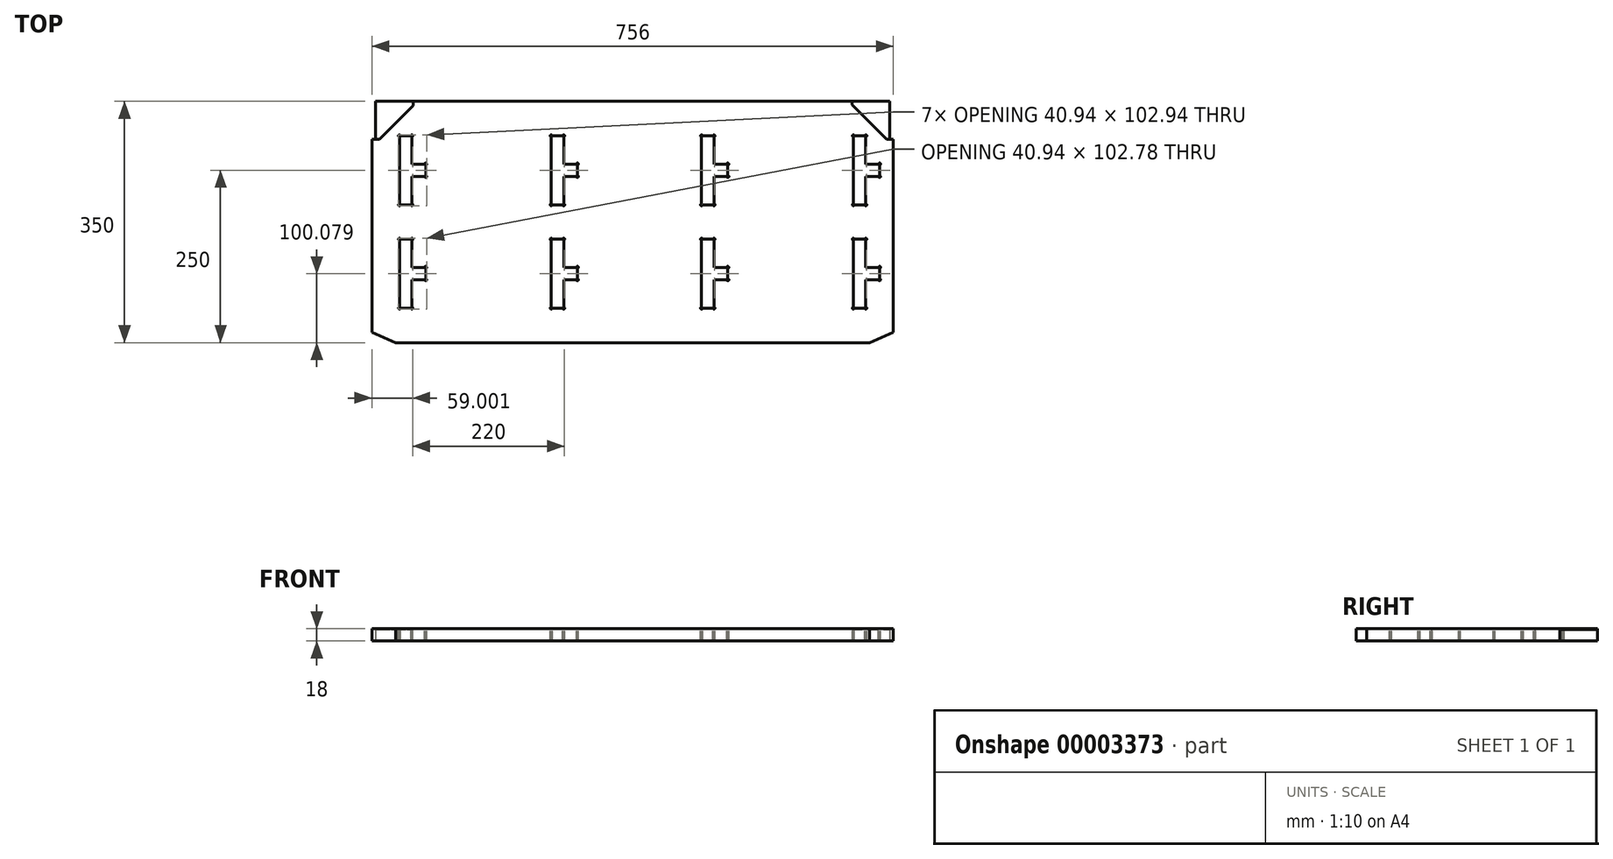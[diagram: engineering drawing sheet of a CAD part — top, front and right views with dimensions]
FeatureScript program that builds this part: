
annotation { "Feature Type Name" : "Feature", "Feature Type Description" : "" }
export const myFeature = defineFeature(function(context is Context, id is Id, definition is map)
    precondition{}
    {
        {
            var Q0;
            Q0=qCreatedBy(makeId("Top.planeOp"),FACE);
            var sketch = newSketch(context, id + "F0", { "sketchPlane" : qUnion([Q0])});
            skLineSegment(sketch, "E0.bottom", {"start": v(-425.74, -50) * mm, "end": v(330.26, -50) * mm});
            skLineSegment(sketch, "E0.top", {"start": v(-420.74, 300) * mm, "end": v(325.26, 300) * mm});
            skLineSegment(sketch, "E0.left", {"start": v(-425.74, -50) * mm, "end": v(-425.74, 245) * mm});
            skLineSegment(sketch, "E0.right", {"start": v(330.26, -50) * mm, "end": v(330.26, 245) * mm});
            skLineSegment(sketch, "E1.bottom", {"start": v(-165.74, 0) * mm, "end": v(-147.74, 0) * mm});
            skLineSegment(sketch, "E1.top", {"start": v(-165.74, 100) * mm, "end": v(-147.74, 100) * mm});
            skLineSegment(sketch, "E1.left", {"start": v(-165.74, 0) * mm, "end": v(-165.74, 100) * mm});
            skLineSegment(sketch, "E1.right", {"start": v(-147.74, 0) * mm, "end": v(-147.74, 41.16) * mm});
            skLineSegment(sketch, "E2.bottom", {"start": v(-165.74, 150) * mm, "end": v(-147.74, 150) * mm});
            skLineSegment(sketch, "E2.top", {"start": v(-165.74, 250) * mm, "end": v(-147.74, 250) * mm});
            skLineSegment(sketch, "E2.left", {"start": v(-165.74, 150) * mm, "end": v(-165.74, 250) * mm});
            skLineSegment(sketch, "E2.right", {"start": v(-147.74, 150) * mm, "end": v(-147.74, 191) * mm});
            skLineSegment(sketch, "E3.bottom", {"start": v(290.26, 0) * mm, "end": v(272.26, 0) * mm});
            skLineSegment(sketch, "E3.top", {"start": v(290.26, 100) * mm, "end": v(272.26, 100) * mm});
            skLineSegment(sketch, "E3.left", {"start": v(290.26, 0) * mm, "end": v(290.26, 41.16) * mm});
            skLineSegment(sketch, "E3.right", {"start": v(272.26, 0) * mm, "end": v(272.26, 100) * mm});
            skLineSegment(sketch, "E4.bottom", {"start": v(272.26, 250) * mm, "end": v(290.26, 250) * mm});
            skLineSegment(sketch, "E4.top", {"start": v(272.26, 150) * mm, "end": v(290.26, 150) * mm});
            skLineSegment(sketch, "E4.left", {"start": v(272.26, 250) * mm, "end": v(272.26, 150) * mm});
            skLineSegment(sketch, "E4.right", {"start": v(290.26, 250) * mm, "end": v(290.26, 209) * mm});
            skLineSegment(sketch, "E5.bottom", {"start": v(52.26, 100) * mm, "end": v(70.26, 100) * mm});
            skLineSegment(sketch, "E5.top", {"start": v(52.26, 0) * mm, "end": v(70.26, 0) * mm});
            skLineSegment(sketch, "E5.left", {"start": v(52.26, 100) * mm, "end": v(52.26, 0) * mm});
            skLineSegment(sketch, "E5.right", {"start": v(70.26, 100) * mm, "end": v(70.26, 59.16) * mm});
            skLineSegment(sketch, "E6.bottom", {"start": v(52.26, 250) * mm, "end": v(70.26, 250) * mm});
            skLineSegment(sketch, "E6.top", {"start": v(52.26, 150) * mm, "end": v(70.26, 150) * mm});
            skLineSegment(sketch, "E6.left", {"start": v(52.26, 250) * mm, "end": v(52.26, 150) * mm});
            skLineSegment(sketch, "E6.right", {"start": v(70.26, 250) * mm, "end": v(70.26, 209) * mm});
            skLineSegment(sketch, "E7.bottom", {"start": v(-385.74, 0.16) * mm, "end": v(-367.74, 0.16) * mm});
            skLineSegment(sketch, "E7.top", {"start": v(-385.74, 100) * mm, "end": v(-367.74, 100) * mm});
            skLineSegment(sketch, "E7.left", {"start": v(-385.74, 0.16) * mm, "end": v(-385.74, 100) * mm});
            skLineSegment(sketch, "E7.right", {"start": v(-367.74, 0.16) * mm, "end": v(-367.74, 41.16) * mm});
            skLineSegment(sketch, "E8.bottom", {"start": v(-385.74, 150) * mm, "end": v(-367.74, 150) * mm});
            skLineSegment(sketch, "E8.top", {"start": v(-385.74, 250) * mm, "end": v(-367.74, 250) * mm});
            skLineSegment(sketch, "E8.left", {"start": v(-385.74, 150) * mm, "end": v(-385.74, 250) * mm});
            skLineSegment(sketch, "E8.right", {"start": v(-367.74, 150) * mm, "end": v(-367.74, 191) * mm});
            skLineSegment(sketch, "E9.bottom", {"start": v(-367.74, 41.16) * mm, "end": v(-347.74, 41.16) * mm});
            skLineSegment(sketch, "E9.top", {"start": v(-367.74, 59.16) * mm, "end": v(-347.74, 59.16) * mm});
            skLineSegment(sketch, "E9.right", {"start": v(-347.74, 41.16) * mm, "end": v(-347.74, 59.16) * mm});
            skLineSegment(sketch, "E10.bottom", {"start": v(-367.74, 191) * mm, "end": v(-347.74, 191) * mm});
            skLineSegment(sketch, "E10.top", {"start": v(-367.74, 209) * mm, "end": v(-347.74, 209) * mm});
            skLineSegment(sketch, "E10.right", {"start": v(-347.74, 191) * mm, "end": v(-347.74, 209) * mm});
            skLineSegment(sketch, "E11.trimOffspring", {"start": v(-367.74, 59.16) * mm, "end": v(-367.74, 100) * mm});
            skLineSegment(sketch, "E12.trimOffspring", {"start": v(-367.74, 209) * mm, "end": v(-367.74, 250) * mm});
            skLineSegment(sketch, "E13.bottom", {"start": v(-147.74, 41.16) * mm, "end": v(-127.74, 41.16) * mm});
            skLineSegment(sketch, "E13.top", {"start": v(-147.74, 59.16) * mm, "end": v(-127.74, 59.16) * mm});
            skLineSegment(sketch, "E13.right", {"start": v(-127.74, 41.16) * mm, "end": v(-127.74, 59.16) * mm});
            skLineSegment(sketch, "E14.bottom", {"start": v(-147.74, 191) * mm, "end": v(-127.74, 191) * mm});
            skLineSegment(sketch, "E14.top", {"start": v(-147.74, 209) * mm, "end": v(-127.74, 209) * mm});
            skLineSegment(sketch, "E14.right", {"start": v(-127.74, 191) * mm, "end": v(-127.74, 209) * mm});
            skLineSegment(sketch, "E15.bottom", {"start": v(70.26, 41.16) * mm, "end": v(90.26, 41.16) * mm});
            skLineSegment(sketch, "E15.top", {"start": v(70.26, 59.16) * mm, "end": v(90.26, 59.16) * mm});
            skLineSegment(sketch, "E15.right", {"start": v(90.26, 41.16) * mm, "end": v(90.26, 59.16) * mm});
            skLineSegment(sketch, "E16.bottom", {"start": v(70.26, 191) * mm, "end": v(90.26, 191) * mm});
            skLineSegment(sketch, "E16.top", {"start": v(70.26, 209) * mm, "end": v(90.26, 209) * mm});
            skLineSegment(sketch, "E16.right", {"start": v(90.26, 191) * mm, "end": v(90.26, 209) * mm});
            skLineSegment(sketch, "E17.bottom", {"start": v(290.26, 41.16) * mm, "end": v(310.26, 41.16) * mm});
            skLineSegment(sketch, "E17.top", {"start": v(290.26, 59.16) * mm, "end": v(310.26, 59.16) * mm});
            skLineSegment(sketch, "E17.right", {"start": v(310.26, 41.16) * mm, "end": v(310.26, 59.16) * mm});
            skLineSegment(sketch, "E18.bottom", {"start": v(290.26, 191) * mm, "end": v(310.26, 191) * mm});
            skLineSegment(sketch, "E18.top", {"start": v(290.26, 209) * mm, "end": v(310.26, 209) * mm});
            skLineSegment(sketch, "E18.right", {"start": v(310.26, 191) * mm, "end": v(310.26, 209) * mm});
            skLineSegment(sketch, "E19.trimOffspring", {"start": v(-147.74, 59.16) * mm, "end": v(-147.74, 100) * mm});
            skLineSegment(sketch, "E20.trimOffspring", {"start": v(-147.74, 209) * mm, "end": v(-147.74, 250) * mm});
            skLineSegment(sketch, "E21.trimOffspring", {"start": v(70.26, 191) * mm, "end": v(70.26, 150) * mm});
            skLineSegment(sketch, "E22.trimOffspring", {"start": v(70.26, 41.16) * mm, "end": v(70.26, 0) * mm});
            skLineSegment(sketch, "E23.trimOffspring", {"start": v(290.26, 59.16) * mm, "end": v(290.26, 100) * mm});
            skLineSegment(sketch, "E24.trimOffspring", {"start": v(290.26, 191) * mm, "end": v(290.26, 150) * mm});
            skLineSegment(sketch, "E25.top", {"start": v(-425.74, 245) * mm, "end": v(-420.74, 245) * mm});
            skLineSegment(sketch, "E25.right", {"start": v(-420.74, 300) * mm, "end": v(-420.74, 245) * mm});
            skLineSegment(sketch, "E26.top", {"start": v(330.26, 245) * mm, "end": v(325.26, 245) * mm});
            skLineSegment(sketch, "E26.right", {"start": v(325.26, 300) * mm, "end": v(325.26, 245) * mm});
            skSolve(sketch);
        }
        {
            var Q0;
            Q0=makeQuery(id+"F0.imprint","IMPRINT",FACE,{"disambiguationData":[TD([[makeQuery(id+"F0.imprint","IMPRINT",EDGE,{"derivedFrom":sQuery(id+"F0.wireOp",EDGE,"E0.bottom")}),1.0]])]});
            extrude(context, id + "F1", {"entities" : qUnion([Q0]), "depth" : 18 * mm});
        }
        {
            var Q0;
            Q0=makeQuery(id+"F1.opExtrude","CAP_FACE",FACE,{"disambiguationData":[OSD([sQuery(id+"F0.wireOp",EDGE,"E0.bottom"),sQuery(id+"F0.wireOp",EDGE,"E0.top"),sQuery(id+"F0.wireOp",EDGE,"E0.left"),sQuery(id+"F0.wireOp",EDGE,"E0.right"),sQuery(id+"F0.wireOp",EDGE,"E1.bottom"),sQuery(id+"F0.wireOp",EDGE,"E1.top"),sQuery(id+"F0.wireOp",EDGE,"E1.left"),sQuery(id+"F0.wireOp",EDGE,"E1.right"),sQuery(id+"F0.wireOp",EDGE,"E2.bottom"),sQuery(id+"F0.wireOp",EDGE,"E2.top"),sQuery(id+"F0.wireOp",EDGE,"E2.left"),sQuery(id+"F0.wireOp",EDGE,"E2.right"),sQuery(id+"F0.wireOp",EDGE,"E3.bottom"),sQuery(id+"F0.wireOp",EDGE,"E3.top"),sQuery(id+"F0.wireOp",EDGE,"E3.left"),sQuery(id+"F0.wireOp",EDGE,"E3.right"),sQuery(id+"F0.wireOp",EDGE,"E4.bottom"),sQuery(id+"F0.wireOp",EDGE,"E4.top"),sQuery(id+"F0.wireOp",EDGE,"E4.left"),sQuery(id+"F0.wireOp",EDGE,"E4.right"),sQuery(id+"F0.wireOp",EDGE,"E5.bottom"),sQuery(id+"F0.wireOp",EDGE,"E5.top"),sQuery(id+"F0.wireOp",EDGE,"E5.left"),sQuery(id+"F0.wireOp",EDGE,"E5.right"),sQuery(id+"F0.wireOp",EDGE,"E6.bottom"),sQuery(id+"F0.wireOp",EDGE,"E6.top"),sQuery(id+"F0.wireOp",EDGE,"E6.left"),sQuery(id+"F0.wireOp",EDGE,"E6.right"),sQuery(id+"F0.wireOp",EDGE,"E7.bottom"),sQuery(id+"F0.wireOp",EDGE,"E7.top"),sQuery(id+"F0.wireOp",EDGE,"E7.left"),sQuery(id+"F0.wireOp",EDGE,"E7.right"),sQuery(id+"F0.wireOp",EDGE,"E8.bottom"),sQuery(id+"F0.wireOp",EDGE,"E8.top"),sQuery(id+"F0.wireOp",EDGE,"E8.left"),sQuery(id+"F0.wireOp",EDGE,"E8.right"),sQuery(id+"F0.wireOp",EDGE,"E9.bottom"),sQuery(id+"F0.wireOp",EDGE,"E9.top"),sQuery(id+"F0.wireOp",EDGE,"E9.right"),sQuery(id+"F0.wireOp",EDGE,"E10.bottom"),sQuery(id+"F0.wireOp",EDGE,"E10.top"),sQuery(id+"F0.wireOp",EDGE,"E10.right"),sQuery(id+"F0.wireOp",EDGE,"E11.trimOffspring"),sQuery(id+"F0.wireOp",EDGE,"E12.trimOffspring"),sQuery(id+"F0.wireOp",EDGE,"E13.bottom"),sQuery(id+"F0.wireOp",EDGE,"E13.top"),sQuery(id+"F0.wireOp",EDGE,"E13.right"),sQuery(id+"F0.wireOp",EDGE,"E14.bottom"),sQuery(id+"F0.wireOp",EDGE,"E14.top"),sQuery(id+"F0.wireOp",EDGE,"E14.right"),sQuery(id+"F0.wireOp",EDGE,"E15.bottom"),sQuery(id+"F0.wireOp",EDGE,"E15.top"),sQuery(id+"F0.wireOp",EDGE,"E15.right"),sQuery(id+"F0.wireOp",EDGE,"E16.bottom"),sQuery(id+"F0.wireOp",EDGE,"E16.top"),sQuery(id+"F0.wireOp",EDGE,"E16.right"),sQuery(id+"F0.wireOp",EDGE,"E17.bottom"),sQuery(id+"F0.wireOp",EDGE,"E17.top"),sQuery(id+"F0.wireOp",EDGE,"E17.right"),sQuery(id+"F0.wireOp",EDGE,"E18.bottom"),sQuery(id+"F0.wireOp",EDGE,"E18.top"),sQuery(id+"F0.wireOp",EDGE,"E18.right"),sQuery(id+"F0.wireOp",EDGE,"E19.trimOffspring"),sQuery(id+"F0.wireOp",EDGE,"E20.trimOffspring"),sQuery(id+"F0.wireOp",EDGE,"E21.trimOffspring"),sQuery(id+"F0.wireOp",EDGE,"E22.trimOffspring"),sQuery(id+"F0.wireOp",EDGE,"E23.trimOffspring"),sQuery(id+"F0.wireOp",EDGE,"E24.trimOffspring"),sQuery(id+"F0.wireOp",EDGE,"E25.top"),sQuery(id+"F0.wireOp",EDGE,"E25.right"),sQuery(id+"F0.wireOp",EDGE,"E26.top"),sQuery(id+"F0.wireOp",EDGE,"E26.right")])],"isStart":false});
            var sketch = newSketch(context, id + "F2", { "sketchPlane" : qUnion([Q0])});
            skLineSegment(sketch, "E27", {"start": v(-420.74, 245) * mm, "end": v(-414.74, 245) * mm});
            skLineSegment(sketch, "E28", {"start": v(-414.74, 245) * mm, "end": v(-365.74, 294) * mm});
            skLineSegment(sketch, "E29", {"start": v(-365.74, 294) * mm, "end": v(-365.74, 300) * mm});
            skLineSegment(sketch, "E30", {"start": v(325.26, 245) * mm, "end": v(320.26, 245) * mm});
            skLineSegment(sketch, "E31", {"start": v(320.26, 245) * mm, "end": v(270.26, 295) * mm});
            skLineSegment(sketch, "E32", {"start": v(270.26, 295) * mm, "end": v(270.26, 300) * mm});
            skSolve(sketch);
        }
        {
            var Q0;
            Q0 = qSketchRegion(id + "F2", true);
            var Q1;
            Q1=makeQuery(id+"F2.imprint","IMPRINT",FACE,{"disambiguationData":[TD([[makeQuery(id+"F2.imprint","IMPRINT",EDGE,{"derivedFrom":sQuery(id+"F2.wireOp",EDGE,"E27")}),1.0]])]});
            var Q2;
            Q2=makeQuery(id+"F2.imprint","IMPRINT",FACE,{"disambiguationData":[TD([[makeQuery(id+"F2.imprint","IMPRINT",EDGE,{"derivedFrom":sQuery(id+"F2.wireOp",EDGE,"E30")}),-1.0]])]});
            extrude(context, id + "F3", {"entities" : qUnion([Q0, Q1, Q2]), "operationType" : NewBodyOperationType.REMOVE, "oppositeDirection" : true, "depth" : 1.5 * mm});
        }
        {
            var Q0;
            Q0=makeQuery(id+"F1.opExtrude","SWEPT_EDGE",EDGE,{"disambiguationData":[OSD([sQuery(id+"F0.wireOp",EDGE,"E0.bottom"),sQuery(id+"F0.wireOp",EDGE,"E0.right")])]});
            var Q1;
            Q1=makeQuery(id+"F1.opExtrude","SWEPT_EDGE",EDGE,{"disambiguationData":[OSD([sQuery(id+"F0.wireOp",EDGE,"E0.bottom"),sQuery(id+"F0.wireOp",EDGE,"E0.left")])]});
            var Q2;
            Q2=makeQuery(id+"F1.opExtrude","SWEPT_EDGE",EDGE,{"disambiguationData":[OSD([sQuery(id+"F0.wireOp",EDGE,"E0.bottom"),sQuery(id+"F0.wireOp",EDGE,"E0.left")])]});
            chamfer(context, id + "F4", {"entities" : qUnion([Q0, Q1, Q2]), "chamferType" : ChamferType.TWO_OFFSETS, "width1" : 15 * mm, "oppositeDirection" : false, "width2" : 34.5 * mm, "tangentPropagation" : true});
        }
        {
            var Q0;
            Q0=makeQuery(id+"F1.opExtrude","CAP_FACE",FACE,{"disambiguationData":[OSD([sQuery(id+"F0.wireOp",EDGE,"E0.bottom"),sQuery(id+"F0.wireOp",EDGE,"E0.top"),sQuery(id+"F0.wireOp",EDGE,"E0.left"),sQuery(id+"F0.wireOp",EDGE,"E0.right"),sQuery(id+"F0.wireOp",EDGE,"E1.bottom"),sQuery(id+"F0.wireOp",EDGE,"E1.top"),sQuery(id+"F0.wireOp",EDGE,"E1.left"),sQuery(id+"F0.wireOp",EDGE,"E1.right"),sQuery(id+"F0.wireOp",EDGE,"E2.bottom"),sQuery(id+"F0.wireOp",EDGE,"E2.top"),sQuery(id+"F0.wireOp",EDGE,"E2.left"),sQuery(id+"F0.wireOp",EDGE,"E2.right"),sQuery(id+"F0.wireOp",EDGE,"E3.bottom"),sQuery(id+"F0.wireOp",EDGE,"E3.top"),sQuery(id+"F0.wireOp",EDGE,"E3.left"),sQuery(id+"F0.wireOp",EDGE,"E3.right"),sQuery(id+"F0.wireOp",EDGE,"E4.bottom"),sQuery(id+"F0.wireOp",EDGE,"E4.top"),sQuery(id+"F0.wireOp",EDGE,"E4.left"),sQuery(id+"F0.wireOp",EDGE,"E4.right"),sQuery(id+"F0.wireOp",EDGE,"E5.bottom"),sQuery(id+"F0.wireOp",EDGE,"E5.top"),sQuery(id+"F0.wireOp",EDGE,"E5.left"),sQuery(id+"F0.wireOp",EDGE,"E5.right"),sQuery(id+"F0.wireOp",EDGE,"E6.bottom"),sQuery(id+"F0.wireOp",EDGE,"E6.top"),sQuery(id+"F0.wireOp",EDGE,"E6.left"),sQuery(id+"F0.wireOp",EDGE,"E6.right"),sQuery(id+"F0.wireOp",EDGE,"E7.bottom"),sQuery(id+"F0.wireOp",EDGE,"E7.top"),sQuery(id+"F0.wireOp",EDGE,"E7.left"),sQuery(id+"F0.wireOp",EDGE,"E7.right"),sQuery(id+"F0.wireOp",EDGE,"E8.bottom"),sQuery(id+"F0.wireOp",EDGE,"E8.top"),sQuery(id+"F0.wireOp",EDGE,"E8.left"),sQuery(id+"F0.wireOp",EDGE,"E8.right"),sQuery(id+"F0.wireOp",EDGE,"E9.bottom"),sQuery(id+"F0.wireOp",EDGE,"E9.top"),sQuery(id+"F0.wireOp",EDGE,"E9.right"),sQuery(id+"F0.wireOp",EDGE,"E10.bottom"),sQuery(id+"F0.wireOp",EDGE,"E10.top"),sQuery(id+"F0.wireOp",EDGE,"E10.right"),sQuery(id+"F0.wireOp",EDGE,"E11.trimOffspring"),sQuery(id+"F0.wireOp",EDGE,"E12.trimOffspring"),sQuery(id+"F0.wireOp",EDGE,"E13.bottom"),sQuery(id+"F0.wireOp",EDGE,"E13.top"),sQuery(id+"F0.wireOp",EDGE,"E13.right"),sQuery(id+"F0.wireOp",EDGE,"E14.bottom"),sQuery(id+"F0.wireOp",EDGE,"E14.top"),sQuery(id+"F0.wireOp",EDGE,"E14.right"),sQuery(id+"F0.wireOp",EDGE,"E15.bottom"),sQuery(id+"F0.wireOp",EDGE,"E15.top"),sQuery(id+"F0.wireOp",EDGE,"E15.right"),sQuery(id+"F0.wireOp",EDGE,"E16.bottom"),sQuery(id+"F0.wireOp",EDGE,"E16.top"),sQuery(id+"F0.wireOp",EDGE,"E16.right"),sQuery(id+"F0.wireOp",EDGE,"E17.bottom"),sQuery(id+"F0.wireOp",EDGE,"E17.top"),sQuery(id+"F0.wireOp",EDGE,"E17.right"),sQuery(id+"F0.wireOp",EDGE,"E18.bottom"),sQuery(id+"F0.wireOp",EDGE,"E18.top"),sQuery(id+"F0.wireOp",EDGE,"E18.right"),sQuery(id+"F0.wireOp",EDGE,"E19.trimOffspring"),sQuery(id+"F0.wireOp",EDGE,"E20.trimOffspring"),sQuery(id+"F0.wireOp",EDGE,"E21.trimOffspring"),sQuery(id+"F0.wireOp",EDGE,"E22.trimOffspring"),sQuery(id+"F0.wireOp",EDGE,"E23.trimOffspring"),sQuery(id+"F0.wireOp",EDGE,"E24.trimOffspring"),sQuery(id+"F0.wireOp",EDGE,"E25.top"),sQuery(id+"F0.wireOp",EDGE,"E25.right"),sQuery(id+"F0.wireOp",EDGE,"E26.top"),sQuery(id+"F0.wireOp",EDGE,"E26.right")])],"isStart":false});
            var sketch = newSketch(context, id + "F5", { "sketchPlane" : qUnion([Q0])});
            skCircle(sketch, "E33", {"center": v(-347.74, 41.16) * mm, "radius": 1.5 * mm});
            skCircle(sketch, "E34", {"center": v(-347.74, 59.16) * mm, "radius": 1.5 * mm});
            skCircle(sketch, "E35", {"center": v(-367.74, 100) * mm, "radius": 1.5 * mm});
            skCircle(sketch, "E36", {"center": v(-385.74, 100) * mm, "radius": 1.5 * mm});
            skCircle(sketch, "E37", {"center": v(-385.74, 0.16) * mm, "radius": 1.5 * mm});
            skCircle(sketch, "E38", {"center": v(-367.74, 0.16) * mm, "radius": 1.5 * mm});
            skCircle(sketch, "E39", {"center": v(-147.74, 0) * mm, "radius": 1.5 * mm});
            skCircle(sketch, "E40", {"center": v(-165.74, 0) * mm, "radius": 1.5 * mm});
            skCircle(sketch, "E41", {"center": v(-165.74, 100) * mm, "radius": 1.5 * mm});
            skCircle(sketch, "E42", {"center": v(-147.74, 100) * mm, "radius": 1.5 * mm});
            skCircle(sketch, "E43", {"center": v(-127.74, 59.16) * mm, "radius": 1.5 * mm});
            skCircle(sketch, "E44", {"center": v(-127.74, 41.16) * mm, "radius": 1.5 * mm});
            skCircle(sketch, "E45", {"center": v(-127.74, 191) * mm, "radius": 1.5 * mm});
            skCircle(sketch, "E46", {"center": v(-127.74, 209) * mm, "radius": 1.5 * mm});
            skCircle(sketch, "E47", {"center": v(-147.74, 250) * mm, "radius": 1.5 * mm});
            skCircle(sketch, "E48", {"center": v(-165.74, 250) * mm, "radius": 1.5 * mm});
            skCircle(sketch, "E49", {"center": v(-165.74, 150) * mm, "radius": 1.5 * mm});
            skCircle(sketch, "E50", {"center": v(-147.74, 150) * mm, "radius": 1.5 * mm});
            skCircle(sketch, "E51", {"center": v(52.26, 100) * mm, "radius": 1.5 * mm});
            skCircle(sketch, "E52", {"center": v(70.26, 100) * mm, "radius": 1.5 * mm});
            skCircle(sketch, "E53", {"center": v(52.26, 0) * mm, "radius": 1.5 * mm});
            skCircle(sketch, "E54", {"center": v(70.26, 0) * mm, "radius": 1.5 * mm});
            skCircle(sketch, "E55", {"center": v(90.26, 41.16) * mm, "radius": 1.5 * mm});
            skCircle(sketch, "E56", {"center": v(90.26, 59.16) * mm, "radius": 1.5 * mm});
            skCircle(sketch, "E57", {"center": v(90.26, 191) * mm, "radius": 1.5 * mm});
            skCircle(sketch, "E58", {"center": v(90.26, 209) * mm, "radius": 1.5 * mm});
            skCircle(sketch, "E59", {"center": v(70.26, 250) * mm, "radius": 1.5 * mm});
            skCircle(sketch, "E60", {"center": v(52.26, 250) * mm, "radius": 1.5 * mm});
            skCircle(sketch, "E61", {"center": v(52.26, 150) * mm, "radius": 1.5 * mm});
            skCircle(sketch, "E62", {"center": v(70.26, 150) * mm, "radius": 1.5 * mm});
            skCircle(sketch, "E63", {"center": v(-367.74, 150) * mm, "radius": 1.5 * mm});
            skCircle(sketch, "E64", {"center": v(-385.74, 150) * mm, "radius": 1.5 * mm});
            skCircle(sketch, "E65", {"center": v(-385.74, 250) * mm, "radius": 1.5 * mm});
            skCircle(sketch, "E66", {"center": v(-367.74, 250) * mm, "radius": 1.5 * mm});
            skCircle(sketch, "E67", {"center": v(-347.74, 209) * mm, "radius": 1.5 * mm});
            skCircle(sketch, "E68", {"center": v(-347.74, 191) * mm, "radius": 1.5 * mm});
            skCircle(sketch, "E69", {"center": v(290.26, 0) * mm, "radius": 1.5 * mm});
            skCircle(sketch, "E70", {"center": v(272.26, 0) * mm, "radius": 1.5 * mm});
            skCircle(sketch, "E71", {"center": v(272.26, 100) * mm, "radius": 1.5 * mm});
            skCircle(sketch, "E72", {"center": v(290.26, 100) * mm, "radius": 1.5 * mm});
            skCircle(sketch, "E73", {"center": v(310.26, 59.16) * mm, "radius": 1.5 * mm});
            skCircle(sketch, "E74", {"center": v(310.26, 41.16) * mm, "radius": 1.5 * mm});
            skCircle(sketch, "E75", {"center": v(310.26, 191) * mm, "radius": 1.5 * mm});
            skCircle(sketch, "E76", {"center": v(310.26, 209) * mm, "radius": 1.5 * mm});
            skCircle(sketch, "E77", {"center": v(290.26, 150) * mm, "radius": 1.5 * mm});
            skCircle(sketch, "E78", {"center": v(272.26, 150) * mm, "radius": 1.5 * mm});
            skCircle(sketch, "E79", {"center": v(272.26, 250) * mm, "radius": 1.5 * mm});
            skCircle(sketch, "E80", {"center": v(290.26, 250) * mm, "radius": 1.5 * mm});
            skSolve(sketch);
        }
        {
            var Q0;
            {var subQ0=makeQuery(id+"F1.opExtrude","CAP_EDGE",EDGE,{"disambiguationData":[OSD([sQuery(id+"F0.wireOp",EDGE,"E9.bottom")])],"isStart":false});var subQ1=sQuery(id+"F5.wireOp",EDGE,"E33");var subQ2=makeQuery(id+"F5.imprint","INTERSECT",VERTEX,{"derivedFrom":[subQ0,subQ1]});var subQ8=sQuery(id+"F5.wireOp",EDGE,"E34");var subQ10=makeQuery(id+"F1.opExtrude","CAP_EDGE",EDGE,{"disambiguationData":[OSD([sQuery(id+"F0.wireOp",EDGE,"E9.top")])],"isStart":false});var subQ13=makeQuery(id+"F5.imprint","INTERSECT",VERTEX,{"derivedFrom":[subQ10,subQ8]});var subQ16=sQuery(id+"F5.wireOp",EDGE,"E35");var subQ18=makeQuery(id+"F1.opExtrude","CAP_EDGE",EDGE,{"disambiguationData":[OSD([sQuery(id+"F0.wireOp",EDGE,"E7.top")])],"isStart":false});var subQ21=makeQuery(id+"F5.imprint","INTERSECT",VERTEX,{"derivedFrom":[subQ18,subQ16]});var subQ24=sQuery(id+"F5.wireOp",EDGE,"E36");var subQ28=makeQuery(id+"F5.imprint","INTERSECT",VERTEX,{"derivedFrom":[subQ18,subQ24]});var subQ30=sQuery(id+"F5.wireOp",EDGE,"E37");var subQ32=makeQuery(id+"F1.opExtrude","CAP_EDGE",EDGE,{"disambiguationData":[OSD([sQuery(id+"F0.wireOp",EDGE,"E7.bottom")])],"isStart":false});var subQ35=makeQuery(id+"F5.imprint","INTERSECT",VERTEX,{"derivedFrom":[subQ32,subQ30]});var subQ37=sQuery(id+"F5.wireOp",EDGE,"E38");var subQ38=makeQuery(id+"F5.imprint","INTERSECT",VERTEX,{"derivedFrom":[subQ32,subQ37]});var subQ45=sQuery(id+"F5.wireOp",EDGE,"E39");var subQ47=makeQuery(id+"F1.opExtrude","CAP_EDGE",EDGE,{"disambiguationData":[OSD([sQuery(id+"F0.wireOp",EDGE,"E1.bottom")])],"isStart":false});var subQ50=makeQuery(id+"F5.imprint","INTERSECT",VERTEX,{"derivedFrom":[subQ47,subQ45]});var subQ52=sQuery(id+"F5.wireOp",EDGE,"E40");var subQ53=makeQuery(id+"F5.imprint","INTERSECT",VERTEX,{"derivedFrom":[subQ47,subQ52]});var subQ59=sQuery(id+"F5.wireOp",EDGE,"E41");var subQ61=makeQuery(id+"F1.opExtrude","CAP_EDGE",EDGE,{"disambiguationData":[OSD([sQuery(id+"F0.wireOp",EDGE,"E1.top")])],"isStart":false});var subQ64=makeQuery(id+"F5.imprint","INTERSECT",VERTEX,{"derivedFrom":[subQ61,subQ59]});var subQ67=sQuery(id+"F5.wireOp",EDGE,"E42");var subQ71=makeQuery(id+"F5.imprint","INTERSECT",VERTEX,{"derivedFrom":[subQ61,subQ67]});var subQ74=sQuery(id+"F5.wireOp",EDGE,"E43");var subQ76=makeQuery(id+"F1.opExtrude","CAP_EDGE",EDGE,{"disambiguationData":[OSD([sQuery(id+"F0.wireOp",EDGE,"E13.top")])],"isStart":false});var subQ79=makeQuery(id+"F5.imprint","INTERSECT",VERTEX,{"derivedFrom":[subQ76,subQ74]});var subQ81=sQuery(id+"F5.wireOp",EDGE,"E44");var subQ83=makeQuery(id+"F1.opExtrude","CAP_EDGE",EDGE,{"disambiguationData":[OSD([sQuery(id+"F0.wireOp",EDGE,"E13.bottom")])],"isStart":false});var subQ86=makeQuery(id+"F5.imprint","INTERSECT",VERTEX,{"derivedFrom":[subQ83,subQ81]});var subQ89=sQuery(id+"F5.wireOp",EDGE,"E45");var subQ91=makeQuery(id+"F1.opExtrude","CAP_EDGE",EDGE,{"disambiguationData":[OSD([sQuery(id+"F0.wireOp",EDGE,"E14.bottom")])],"isStart":false});var subQ94=makeQuery(id+"F5.imprint","INTERSECT",VERTEX,{"derivedFrom":[subQ91,subQ89]});var subQ96=sQuery(id+"F5.wireOp",EDGE,"E46");var subQ98=makeQuery(id+"F1.opExtrude","CAP_EDGE",EDGE,{"disambiguationData":[OSD([sQuery(id+"F0.wireOp",EDGE,"E14.top")])],"isStart":false});var subQ101=makeQuery(id+"F5.imprint","INTERSECT",VERTEX,{"derivedFrom":[subQ98,subQ96]});var subQ104=sQuery(id+"F5.wireOp",EDGE,"E47");var subQ106=makeQuery(id+"F1.opExtrude","CAP_EDGE",EDGE,{"disambiguationData":[OSD([sQuery(id+"F0.wireOp",EDGE,"E2.top")])],"isStart":false});var subQ109=makeQuery(id+"F5.imprint","INTERSECT",VERTEX,{"derivedFrom":[subQ106,subQ104]});var subQ112=sQuery(id+"F5.wireOp",EDGE,"E48");var subQ116=makeQuery(id+"F5.imprint","INTERSECT",VERTEX,{"derivedFrom":[subQ106,subQ112]});var subQ118=sQuery(id+"F5.wireOp",EDGE,"E49");var subQ120=makeQuery(id+"F1.opExtrude","CAP_EDGE",EDGE,{"disambiguationData":[OSD([sQuery(id+"F0.wireOp",EDGE,"E2.bottom")])],"isStart":false});var subQ123=makeQuery(id+"F5.imprint","INTERSECT",VERTEX,{"derivedFrom":[subQ120,subQ118]});var subQ126=sQuery(id+"F5.wireOp",EDGE,"E50");var subQ130=makeQuery(id+"F5.imprint","INTERSECT",VERTEX,{"derivedFrom":[subQ120,subQ126]});var subQ133=sQuery(id+"F5.wireOp",EDGE,"E51");var subQ135=makeQuery(id+"F1.opExtrude","CAP_EDGE",EDGE,{"disambiguationData":[OSD([sQuery(id+"F0.wireOp",EDGE,"E5.bottom")])],"isStart":false});var subQ138=makeQuery(id+"F5.imprint","INTERSECT",VERTEX,{"derivedFrom":[subQ135,subQ133]});var subQ141=sQuery(id+"F5.wireOp",EDGE,"E52");var subQ145=makeQuery(id+"F5.imprint","INTERSECT",VERTEX,{"derivedFrom":[subQ135,subQ141]});var subQ147=sQuery(id+"F5.wireOp",EDGE,"E53");var subQ149=makeQuery(id+"F1.opExtrude","CAP_EDGE",EDGE,{"disambiguationData":[OSD([sQuery(id+"F0.wireOp",EDGE,"E5.top")])],"isStart":false});var subQ152=makeQuery(id+"F5.imprint","INTERSECT",VERTEX,{"derivedFrom":[subQ149,subQ147]});var subQ155=sQuery(id+"F5.wireOp",EDGE,"E54");var subQ159=makeQuery(id+"F5.imprint","INTERSECT",VERTEX,{"derivedFrom":[subQ149,subQ155]});var subQ162=sQuery(id+"F5.wireOp",EDGE,"E55");var subQ164=makeQuery(id+"F1.opExtrude","CAP_EDGE",EDGE,{"disambiguationData":[OSD([sQuery(id+"F0.wireOp",EDGE,"E15.bottom")])],"isStart":false});var subQ167=makeQuery(id+"F5.imprint","INTERSECT",VERTEX,{"derivedFrom":[subQ164,subQ162]});var subQ169=sQuery(id+"F5.wireOp",EDGE,"E56");var subQ171=makeQuery(id+"F1.opExtrude","CAP_EDGE",EDGE,{"disambiguationData":[OSD([sQuery(id+"F0.wireOp",EDGE,"E15.top")])],"isStart":false});var subQ174=makeQuery(id+"F5.imprint","INTERSECT",VERTEX,{"derivedFrom":[subQ171,subQ169]});var subQ177=sQuery(id+"F5.wireOp",EDGE,"E57");var subQ179=makeQuery(id+"F1.opExtrude","CAP_EDGE",EDGE,{"disambiguationData":[OSD([sQuery(id+"F0.wireOp",EDGE,"E16.bottom")])],"isStart":false});var subQ182=makeQuery(id+"F5.imprint","INTERSECT",VERTEX,{"derivedFrom":[subQ179,subQ177]});var subQ184=sQuery(id+"F5.wireOp",EDGE,"E58");var subQ186=makeQuery(id+"F1.opExtrude","CAP_EDGE",EDGE,{"disambiguationData":[OSD([sQuery(id+"F0.wireOp",EDGE,"E16.top")])],"isStart":false});var subQ189=makeQuery(id+"F5.imprint","INTERSECT",VERTEX,{"derivedFrom":[subQ186,subQ184]});var subQ192=sQuery(id+"F5.wireOp",EDGE,"E59");var subQ194=makeQuery(id+"F1.opExtrude","CAP_EDGE",EDGE,{"disambiguationData":[OSD([sQuery(id+"F0.wireOp",EDGE,"E6.bottom")])],"isStart":false});var subQ197=makeQuery(id+"F5.imprint","INTERSECT",VERTEX,{"derivedFrom":[subQ194,subQ192]});var subQ200=sQuery(id+"F5.wireOp",EDGE,"E60");var subQ204=makeQuery(id+"F5.imprint","INTERSECT",VERTEX,{"derivedFrom":[subQ194,subQ200]});var subQ206=sQuery(id+"F5.wireOp",EDGE,"E61");var subQ208=makeQuery(id+"F1.opExtrude","CAP_EDGE",EDGE,{"disambiguationData":[OSD([sQuery(id+"F0.wireOp",EDGE,"E6.top")])],"isStart":false});var subQ211=makeQuery(id+"F5.imprint","INTERSECT",VERTEX,{"derivedFrom":[subQ208,subQ206]});var subQ214=sQuery(id+"F5.wireOp",EDGE,"E62");var subQ218=makeQuery(id+"F5.imprint","INTERSECT",VERTEX,{"derivedFrom":[subQ208,subQ214]});var subQ221=sQuery(id+"F5.wireOp",EDGE,"E63");var subQ223=makeQuery(id+"F1.opExtrude","CAP_EDGE",EDGE,{"disambiguationData":[OSD([sQuery(id+"F0.wireOp",EDGE,"E8.bottom")])],"isStart":false});var subQ226=makeQuery(id+"F5.imprint","INTERSECT",VERTEX,{"derivedFrom":[subQ223,subQ221]});var subQ229=sQuery(id+"F5.wireOp",EDGE,"E64");var subQ233=makeQuery(id+"F5.imprint","INTERSECT",VERTEX,{"derivedFrom":[subQ223,subQ229]});var subQ235=sQuery(id+"F5.wireOp",EDGE,"E65");var subQ237=makeQuery(id+"F1.opExtrude","CAP_EDGE",EDGE,{"disambiguationData":[OSD([sQuery(id+"F0.wireOp",EDGE,"E8.top")])],"isStart":false});var subQ240=makeQuery(id+"F5.imprint","INTERSECT",VERTEX,{"derivedFrom":[subQ237,subQ235]});var subQ243=sQuery(id+"F5.wireOp",EDGE,"E66");var subQ247=makeQuery(id+"F5.imprint","INTERSECT",VERTEX,{"derivedFrom":[subQ237,subQ243]});var subQ250=sQuery(id+"F5.wireOp",EDGE,"E67");var subQ252=makeQuery(id+"F1.opExtrude","CAP_EDGE",EDGE,{"disambiguationData":[OSD([sQuery(id+"F0.wireOp",EDGE,"E10.top")])],"isStart":false});var subQ255=makeQuery(id+"F5.imprint","INTERSECT",VERTEX,{"derivedFrom":[subQ252,subQ250]});var subQ257=makeQuery(id+"F1.opExtrude","CAP_EDGE",EDGE,{"disambiguationData":[OSD([sQuery(id+"F0.wireOp",EDGE,"E10.bottom")])],"isStart":false});var subQ258=sQuery(id+"F5.wireOp",EDGE,"E68");var subQ259=makeQuery(id+"F5.imprint","INTERSECT",VERTEX,{"derivedFrom":[subQ257,subQ258]});var subQ265=sQuery(id+"F5.wireOp",EDGE,"E69");var subQ267=makeQuery(id+"F1.opExtrude","CAP_EDGE",EDGE,{"disambiguationData":[OSD([sQuery(id+"F0.wireOp",EDGE,"E3.bottom")])],"isStart":false});var subQ270=makeQuery(id+"F5.imprint","INTERSECT",VERTEX,{"derivedFrom":[subQ267,subQ265]});var subQ273=sQuery(id+"F5.wireOp",EDGE,"E70");var subQ277=makeQuery(id+"F5.imprint","INTERSECT",VERTEX,{"derivedFrom":[subQ267,subQ273]});var subQ279=sQuery(id+"F5.wireOp",EDGE,"E71");var subQ281=makeQuery(id+"F1.opExtrude","CAP_EDGE",EDGE,{"disambiguationData":[OSD([sQuery(id+"F0.wireOp",EDGE,"E3.top")])],"isStart":false});var subQ284=makeQuery(id+"F5.imprint","INTERSECT",VERTEX,{"derivedFrom":[subQ281,subQ279]});var subQ287=sQuery(id+"F5.wireOp",EDGE,"E72");var subQ291=makeQuery(id+"F5.imprint","INTERSECT",VERTEX,{"derivedFrom":[subQ281,subQ287]});var subQ294=sQuery(id+"F5.wireOp",EDGE,"E73");var subQ296=makeQuery(id+"F1.opExtrude","CAP_EDGE",EDGE,{"disambiguationData":[OSD([sQuery(id+"F0.wireOp",EDGE,"E17.top")])],"isStart":false});var subQ299=makeQuery(id+"F5.imprint","INTERSECT",VERTEX,{"derivedFrom":[subQ296,subQ294]});var subQ301=sQuery(id+"F5.wireOp",EDGE,"E74");var subQ303=makeQuery(id+"F1.opExtrude","CAP_EDGE",EDGE,{"disambiguationData":[OSD([sQuery(id+"F0.wireOp",EDGE,"E17.bottom")])],"isStart":false});var subQ306=makeQuery(id+"F5.imprint","INTERSECT",VERTEX,{"derivedFrom":[subQ303,subQ301]});var subQ309=sQuery(id+"F5.wireOp",EDGE,"E75");var subQ311=makeQuery(id+"F1.opExtrude","CAP_EDGE",EDGE,{"disambiguationData":[OSD([sQuery(id+"F0.wireOp",EDGE,"E18.bottom")])],"isStart":false});var subQ314=makeQuery(id+"F5.imprint","INTERSECT",VERTEX,{"derivedFrom":[subQ311,subQ309]});var subQ316=sQuery(id+"F5.wireOp",EDGE,"E76");var subQ318=makeQuery(id+"F1.opExtrude","CAP_EDGE",EDGE,{"disambiguationData":[OSD([sQuery(id+"F0.wireOp",EDGE,"E18.top")])],"isStart":false});var subQ321=makeQuery(id+"F5.imprint","INTERSECT",VERTEX,{"derivedFrom":[subQ318,subQ316]});var subQ324=sQuery(id+"F5.wireOp",EDGE,"E77");var subQ326=makeQuery(id+"F1.opExtrude","CAP_EDGE",EDGE,{"disambiguationData":[OSD([sQuery(id+"F0.wireOp",EDGE,"E4.top")])],"isStart":false});var subQ329=makeQuery(id+"F5.imprint","INTERSECT",VERTEX,{"derivedFrom":[subQ326,subQ324]});var subQ332=sQuery(id+"F5.wireOp",EDGE,"E78");var subQ336=makeQuery(id+"F5.imprint","INTERSECT",VERTEX,{"derivedFrom":[subQ326,subQ332]});var subQ338=sQuery(id+"F5.wireOp",EDGE,"E79");var subQ340=makeQuery(id+"F1.opExtrude","CAP_EDGE",EDGE,{"disambiguationData":[OSD([sQuery(id+"F0.wireOp",EDGE,"E4.bottom")])],"isStart":false});var subQ343=makeQuery(id+"F5.imprint","INTERSECT",VERTEX,{"derivedFrom":[subQ340,subQ338]});var subQ346=sQuery(id+"F5.wireOp",EDGE,"E80");var subQ350=makeQuery(id+"F5.imprint","INTERSECT",VERTEX,{"derivedFrom":[subQ340,subQ346]});Q0=qUnion([makeQuery(id+"F5.imprint","IMPRINT",FACE,{"disambiguationData":[TD([[makeQuery(id+"F5.imprint","IMPRINT",EDGE,{"disambiguationData":[TD([[subQ2,1.0]])],"derivedFrom":subQ1}),1.0]])]}),makeQuery(id+"F5.imprint","IMPRINT",FACE,{"disambiguationData":[TD([[makeQuery(id+"F5.imprint","IMPRINT",EDGE,{"disambiguationData":[TD([[subQ2,-1.0]])],"derivedFrom":subQ1}),1.0]])]}),makeQuery(id+"F5.imprint","IMPRINT",FACE,{"disambiguationData":[TD([[makeQuery(id+"F5.imprint","IMPRINT",EDGE,{"disambiguationData":[TD([[subQ13,-1.0]])],"derivedFrom":subQ8}),1.0]])]}),makeQuery(id+"F5.imprint","IMPRINT",FACE,{"disambiguationData":[TD([[makeQuery(id+"F5.imprint","IMPRINT",EDGE,{"disambiguationData":[TD([[subQ13,1.0]])],"derivedFrom":subQ8}),1.0]])]}),makeQuery(id+"F5.imprint","IMPRINT",FACE,{"disambiguationData":[TD([[makeQuery(id+"F5.imprint","IMPRINT",EDGE,{"disambiguationData":[TD([[subQ21,-1.0]])],"derivedFrom":subQ16}),1.0]])]}),makeQuery(id+"F5.imprint","IMPRINT",FACE,{"disambiguationData":[TD([[makeQuery(id+"F5.imprint","IMPRINT",EDGE,{"disambiguationData":[TD([[subQ21,1.0]])],"derivedFrom":subQ16}),1.0]])]}),makeQuery(id+"F5.imprint","IMPRINT",FACE,{"disambiguationData":[TD([[makeQuery(id+"F5.imprint","IMPRINT",EDGE,{"disambiguationData":[TD([[subQ28,-1.0]])],"derivedFrom":subQ24}),1.0]])]}),makeQuery(id+"F5.imprint","IMPRINT",FACE,{"disambiguationData":[TD([[makeQuery(id+"F5.imprint","IMPRINT",EDGE,{"disambiguationData":[TD([[subQ28,1.0]])],"derivedFrom":subQ24}),1.0]])]}),makeQuery(id+"F5.imprint","IMPRINT",FACE,{"disambiguationData":[TD([[makeQuery(id+"F5.imprint","IMPRINT",EDGE,{"disambiguationData":[TD([[subQ35,-1.0]])],"derivedFrom":subQ30}),1.0]])]}),makeQuery(id+"F5.imprint","IMPRINT",FACE,{"disambiguationData":[TD([[makeQuery(id+"F5.imprint","IMPRINT",EDGE,{"disambiguationData":[TD([[subQ35,1.0]])],"derivedFrom":subQ30}),1.0]])]}),makeQuery(id+"F5.imprint","IMPRINT",FACE,{"disambiguationData":[TD([[makeQuery(id+"F5.imprint","IMPRINT",EDGE,{"disambiguationData":[TD([[subQ38,1.0]])],"derivedFrom":subQ37}),1.0]])]}),makeQuery(id+"F5.imprint","IMPRINT",FACE,{"disambiguationData":[TD([[makeQuery(id+"F5.imprint","IMPRINT",EDGE,{"disambiguationData":[TD([[subQ38,-1.0]])],"derivedFrom":subQ37}),1.0]])]}),makeQuery(id+"F5.imprint","IMPRINT",FACE,{"disambiguationData":[TD([[makeQuery(id+"F5.imprint","IMPRINT",EDGE,{"disambiguationData":[TD([[subQ50,1.0]])],"derivedFrom":subQ45}),1.0]])]}),makeQuery(id+"F5.imprint","IMPRINT",FACE,{"disambiguationData":[TD([[makeQuery(id+"F5.imprint","IMPRINT",EDGE,{"disambiguationData":[TD([[subQ50,-1.0]])],"derivedFrom":subQ45}),1.0]])]}),makeQuery(id+"F5.imprint","IMPRINT",FACE,{"disambiguationData":[TD([[makeQuery(id+"F5.imprint","IMPRINT",EDGE,{"disambiguationData":[TD([[subQ53,-1.0]])],"derivedFrom":subQ52}),1.0]])]}),makeQuery(id+"F5.imprint","IMPRINT",FACE,{"disambiguationData":[TD([[makeQuery(id+"F5.imprint","IMPRINT",EDGE,{"disambiguationData":[TD([[subQ53,1.0]])],"derivedFrom":subQ52}),1.0]])]}),makeQuery(id+"F5.imprint","IMPRINT",FACE,{"disambiguationData":[TD([[makeQuery(id+"F5.imprint","IMPRINT",EDGE,{"disambiguationData":[TD([[subQ64,-1.0]])],"derivedFrom":subQ59}),1.0]])]}),makeQuery(id+"F5.imprint","IMPRINT",FACE,{"disambiguationData":[TD([[makeQuery(id+"F5.imprint","IMPRINT",EDGE,{"disambiguationData":[TD([[subQ64,1.0]])],"derivedFrom":subQ59}),1.0]])]}),makeQuery(id+"F5.imprint","IMPRINT",FACE,{"disambiguationData":[TD([[makeQuery(id+"F5.imprint","IMPRINT",EDGE,{"disambiguationData":[TD([[subQ71,-1.0]])],"derivedFrom":subQ67}),1.0]])]}),makeQuery(id+"F5.imprint","IMPRINT",FACE,{"disambiguationData":[TD([[makeQuery(id+"F5.imprint","IMPRINT",EDGE,{"disambiguationData":[TD([[subQ71,1.0]])],"derivedFrom":subQ67}),1.0]])]}),makeQuery(id+"F5.imprint","IMPRINT",FACE,{"disambiguationData":[TD([[makeQuery(id+"F5.imprint","IMPRINT",EDGE,{"disambiguationData":[TD([[subQ79,-1.0]])],"derivedFrom":subQ74}),1.0]])]}),makeQuery(id+"F5.imprint","IMPRINT",FACE,{"disambiguationData":[TD([[makeQuery(id+"F5.imprint","IMPRINT",EDGE,{"disambiguationData":[TD([[subQ79,1.0]])],"derivedFrom":subQ74}),1.0]])]}),makeQuery(id+"F5.imprint","IMPRINT",FACE,{"disambiguationData":[TD([[makeQuery(id+"F5.imprint","IMPRINT",EDGE,{"disambiguationData":[TD([[subQ86,1.0]])],"derivedFrom":subQ81}),1.0]])]}),makeQuery(id+"F5.imprint","IMPRINT",FACE,{"disambiguationData":[TD([[makeQuery(id+"F5.imprint","IMPRINT",EDGE,{"disambiguationData":[TD([[subQ86,-1.0]])],"derivedFrom":subQ81}),1.0]])]}),makeQuery(id+"F5.imprint","IMPRINT",FACE,{"disambiguationData":[TD([[makeQuery(id+"F5.imprint","IMPRINT",EDGE,{"disambiguationData":[TD([[subQ94,1.0]])],"derivedFrom":subQ89}),1.0]])]}),makeQuery(id+"F5.imprint","IMPRINT",FACE,{"disambiguationData":[TD([[makeQuery(id+"F5.imprint","IMPRINT",EDGE,{"disambiguationData":[TD([[subQ94,-1.0]])],"derivedFrom":subQ89}),1.0]])]}),makeQuery(id+"F5.imprint","IMPRINT",FACE,{"disambiguationData":[TD([[makeQuery(id+"F5.imprint","IMPRINT",EDGE,{"disambiguationData":[TD([[subQ101,-1.0]])],"derivedFrom":subQ96}),1.0]])]}),makeQuery(id+"F5.imprint","IMPRINT",FACE,{"disambiguationData":[TD([[makeQuery(id+"F5.imprint","IMPRINT",EDGE,{"disambiguationData":[TD([[subQ101,1.0]])],"derivedFrom":subQ96}),1.0]])]}),makeQuery(id+"F5.imprint","IMPRINT",FACE,{"disambiguationData":[TD([[makeQuery(id+"F5.imprint","IMPRINT",EDGE,{"disambiguationData":[TD([[subQ109,-1.0]])],"derivedFrom":subQ104}),1.0]])]}),makeQuery(id+"F5.imprint","IMPRINT",FACE,{"disambiguationData":[TD([[makeQuery(id+"F5.imprint","IMPRINT",EDGE,{"disambiguationData":[TD([[subQ109,1.0]])],"derivedFrom":subQ104}),1.0]])]}),makeQuery(id+"F5.imprint","IMPRINT",FACE,{"disambiguationData":[TD([[makeQuery(id+"F5.imprint","IMPRINT",EDGE,{"disambiguationData":[TD([[subQ116,-1.0]])],"derivedFrom":subQ112}),1.0]])]}),makeQuery(id+"F5.imprint","IMPRINT",FACE,{"disambiguationData":[TD([[makeQuery(id+"F5.imprint","IMPRINT",EDGE,{"disambiguationData":[TD([[subQ116,1.0]])],"derivedFrom":subQ112}),1.0]])]}),makeQuery(id+"F5.imprint","IMPRINT",FACE,{"disambiguationData":[TD([[makeQuery(id+"F5.imprint","IMPRINT",EDGE,{"disambiguationData":[TD([[subQ123,-1.0]])],"derivedFrom":subQ118}),1.0]])]}),makeQuery(id+"F5.imprint","IMPRINT",FACE,{"disambiguationData":[TD([[makeQuery(id+"F5.imprint","IMPRINT",EDGE,{"disambiguationData":[TD([[subQ123,1.0]])],"derivedFrom":subQ118}),1.0]])]}),makeQuery(id+"F5.imprint","IMPRINT",FACE,{"disambiguationData":[TD([[makeQuery(id+"F5.imprint","IMPRINT",EDGE,{"disambiguationData":[TD([[subQ130,1.0]])],"derivedFrom":subQ126}),1.0]])]}),makeQuery(id+"F5.imprint","IMPRINT",FACE,{"disambiguationData":[TD([[makeQuery(id+"F5.imprint","IMPRINT",EDGE,{"disambiguationData":[TD([[subQ130,-1.0]])],"derivedFrom":subQ126}),1.0]])]}),makeQuery(id+"F5.imprint","IMPRINT",FACE,{"disambiguationData":[TD([[makeQuery(id+"F5.imprint","IMPRINT",EDGE,{"disambiguationData":[TD([[subQ138,-1.0]])],"derivedFrom":subQ133}),1.0]])]}),makeQuery(id+"F5.imprint","IMPRINT",FACE,{"disambiguationData":[TD([[makeQuery(id+"F5.imprint","IMPRINT",EDGE,{"disambiguationData":[TD([[subQ138,1.0]])],"derivedFrom":subQ133}),1.0]])]}),makeQuery(id+"F5.imprint","IMPRINT",FACE,{"disambiguationData":[TD([[makeQuery(id+"F5.imprint","IMPRINT",EDGE,{"disambiguationData":[TD([[subQ145,-1.0]])],"derivedFrom":subQ141}),1.0]])]}),makeQuery(id+"F5.imprint","IMPRINT",FACE,{"disambiguationData":[TD([[makeQuery(id+"F5.imprint","IMPRINT",EDGE,{"disambiguationData":[TD([[subQ145,1.0]])],"derivedFrom":subQ141}),1.0]])]}),makeQuery(id+"F5.imprint","IMPRINT",FACE,{"disambiguationData":[TD([[makeQuery(id+"F5.imprint","IMPRINT",EDGE,{"disambiguationData":[TD([[subQ152,-1.0]])],"derivedFrom":subQ147}),1.0]])]}),makeQuery(id+"F5.imprint","IMPRINT",FACE,{"disambiguationData":[TD([[makeQuery(id+"F5.imprint","IMPRINT",EDGE,{"disambiguationData":[TD([[subQ152,1.0]])],"derivedFrom":subQ147}),1.0]])]}),makeQuery(id+"F5.imprint","IMPRINT",FACE,{"disambiguationData":[TD([[makeQuery(id+"F5.imprint","IMPRINT",EDGE,{"disambiguationData":[TD([[subQ159,1.0]])],"derivedFrom":subQ155}),1.0]])]}),makeQuery(id+"F5.imprint","IMPRINT",FACE,{"disambiguationData":[TD([[makeQuery(id+"F5.imprint","IMPRINT",EDGE,{"disambiguationData":[TD([[subQ159,-1.0]])],"derivedFrom":subQ155}),1.0]])]}),makeQuery(id+"F5.imprint","IMPRINT",FACE,{"disambiguationData":[TD([[makeQuery(id+"F5.imprint","IMPRINT",EDGE,{"disambiguationData":[TD([[subQ167,1.0]])],"derivedFrom":subQ162}),1.0]])]}),makeQuery(id+"F5.imprint","IMPRINT",FACE,{"disambiguationData":[TD([[makeQuery(id+"F5.imprint","IMPRINT",EDGE,{"disambiguationData":[TD([[subQ167,-1.0]])],"derivedFrom":subQ162}),1.0]])]}),makeQuery(id+"F5.imprint","IMPRINT",FACE,{"disambiguationData":[TD([[makeQuery(id+"F5.imprint","IMPRINT",EDGE,{"disambiguationData":[TD([[subQ174,-1.0]])],"derivedFrom":subQ169}),1.0]])]}),makeQuery(id+"F5.imprint","IMPRINT",FACE,{"disambiguationData":[TD([[makeQuery(id+"F5.imprint","IMPRINT",EDGE,{"disambiguationData":[TD([[subQ174,1.0]])],"derivedFrom":subQ169}),1.0]])]}),makeQuery(id+"F5.imprint","IMPRINT",FACE,{"disambiguationData":[TD([[makeQuery(id+"F5.imprint","IMPRINT",EDGE,{"disambiguationData":[TD([[subQ182,1.0]])],"derivedFrom":subQ177}),1.0]])]}),makeQuery(id+"F5.imprint","IMPRINT",FACE,{"disambiguationData":[TD([[makeQuery(id+"F5.imprint","IMPRINT",EDGE,{"disambiguationData":[TD([[subQ182,-1.0]])],"derivedFrom":subQ177}),1.0]])]}),makeQuery(id+"F5.imprint","IMPRINT",FACE,{"disambiguationData":[TD([[makeQuery(id+"F5.imprint","IMPRINT",EDGE,{"disambiguationData":[TD([[subQ189,-1.0]])],"derivedFrom":subQ184}),1.0]])]}),makeQuery(id+"F5.imprint","IMPRINT",FACE,{"disambiguationData":[TD([[makeQuery(id+"F5.imprint","IMPRINT",EDGE,{"disambiguationData":[TD([[subQ189,1.0]])],"derivedFrom":subQ184}),1.0]])]}),makeQuery(id+"F5.imprint","IMPRINT",FACE,{"disambiguationData":[TD([[makeQuery(id+"F5.imprint","IMPRINT",EDGE,{"disambiguationData":[TD([[subQ197,-1.0]])],"derivedFrom":subQ192}),1.0]])]}),makeQuery(id+"F5.imprint","IMPRINT",FACE,{"disambiguationData":[TD([[makeQuery(id+"F5.imprint","IMPRINT",EDGE,{"disambiguationData":[TD([[subQ197,1.0]])],"derivedFrom":subQ192}),1.0]])]}),makeQuery(id+"F5.imprint","IMPRINT",FACE,{"disambiguationData":[TD([[makeQuery(id+"F5.imprint","IMPRINT",EDGE,{"disambiguationData":[TD([[subQ204,-1.0]])],"derivedFrom":subQ200}),1.0]])]}),makeQuery(id+"F5.imprint","IMPRINT",FACE,{"disambiguationData":[TD([[makeQuery(id+"F5.imprint","IMPRINT",EDGE,{"disambiguationData":[TD([[subQ204,1.0]])],"derivedFrom":subQ200}),1.0]])]}),makeQuery(id+"F5.imprint","IMPRINT",FACE,{"disambiguationData":[TD([[makeQuery(id+"F5.imprint","IMPRINT",EDGE,{"disambiguationData":[TD([[subQ211,-1.0]])],"derivedFrom":subQ206}),1.0]])]}),makeQuery(id+"F5.imprint","IMPRINT",FACE,{"disambiguationData":[TD([[makeQuery(id+"F5.imprint","IMPRINT",EDGE,{"disambiguationData":[TD([[subQ211,1.0]])],"derivedFrom":subQ206}),1.0]])]}),makeQuery(id+"F5.imprint","IMPRINT",FACE,{"disambiguationData":[TD([[makeQuery(id+"F5.imprint","IMPRINT",EDGE,{"disambiguationData":[TD([[subQ218,1.0]])],"derivedFrom":subQ214}),1.0]])]}),makeQuery(id+"F5.imprint","IMPRINT",FACE,{"disambiguationData":[TD([[makeQuery(id+"F5.imprint","IMPRINT",EDGE,{"disambiguationData":[TD([[subQ218,-1.0]])],"derivedFrom":subQ214}),1.0]])]}),makeQuery(id+"F5.imprint","IMPRINT",FACE,{"disambiguationData":[TD([[makeQuery(id+"F5.imprint","IMPRINT",EDGE,{"disambiguationData":[TD([[subQ226,1.0]])],"derivedFrom":subQ221}),1.0]])]}),makeQuery(id+"F5.imprint","IMPRINT",FACE,{"disambiguationData":[TD([[makeQuery(id+"F5.imprint","IMPRINT",EDGE,{"disambiguationData":[TD([[subQ226,-1.0]])],"derivedFrom":subQ221}),1.0]])]}),makeQuery(id+"F5.imprint","IMPRINT",FACE,{"disambiguationData":[TD([[makeQuery(id+"F5.imprint","IMPRINT",EDGE,{"disambiguationData":[TD([[subQ233,-1.0]])],"derivedFrom":subQ229}),1.0]])]}),makeQuery(id+"F5.imprint","IMPRINT",FACE,{"disambiguationData":[TD([[makeQuery(id+"F5.imprint","IMPRINT",EDGE,{"disambiguationData":[TD([[subQ233,1.0]])],"derivedFrom":subQ229}),1.0]])]}),makeQuery(id+"F5.imprint","IMPRINT",FACE,{"disambiguationData":[TD([[makeQuery(id+"F5.imprint","IMPRINT",EDGE,{"disambiguationData":[TD([[subQ240,-1.0]])],"derivedFrom":subQ235}),1.0]])]}),makeQuery(id+"F5.imprint","IMPRINT",FACE,{"disambiguationData":[TD([[makeQuery(id+"F5.imprint","IMPRINT",EDGE,{"disambiguationData":[TD([[subQ240,1.0]])],"derivedFrom":subQ235}),1.0]])]}),makeQuery(id+"F5.imprint","IMPRINT",FACE,{"disambiguationData":[TD([[makeQuery(id+"F5.imprint","IMPRINT",EDGE,{"disambiguationData":[TD([[subQ247,-1.0]])],"derivedFrom":subQ243}),1.0]])]}),makeQuery(id+"F5.imprint","IMPRINT",FACE,{"disambiguationData":[TD([[makeQuery(id+"F5.imprint","IMPRINT",EDGE,{"disambiguationData":[TD([[subQ247,1.0]])],"derivedFrom":subQ243}),1.0]])]}),makeQuery(id+"F5.imprint","IMPRINT",FACE,{"disambiguationData":[TD([[makeQuery(id+"F5.imprint","IMPRINT",EDGE,{"disambiguationData":[TD([[subQ255,-1.0]])],"derivedFrom":subQ250}),1.0]])]}),makeQuery(id+"F5.imprint","IMPRINT",FACE,{"disambiguationData":[TD([[makeQuery(id+"F5.imprint","IMPRINT",EDGE,{"disambiguationData":[TD([[subQ255,1.0]])],"derivedFrom":subQ250}),1.0]])]}),makeQuery(id+"F5.imprint","IMPRINT",FACE,{"disambiguationData":[TD([[makeQuery(id+"F5.imprint","IMPRINT",EDGE,{"disambiguationData":[TD([[subQ259,1.0]])],"derivedFrom":subQ258}),1.0]])]}),makeQuery(id+"F5.imprint","IMPRINT",FACE,{"disambiguationData":[TD([[makeQuery(id+"F5.imprint","IMPRINT",EDGE,{"disambiguationData":[TD([[subQ259,-1.0]])],"derivedFrom":subQ258}),1.0]])]}),makeQuery(id+"F5.imprint","IMPRINT",FACE,{"disambiguationData":[TD([[makeQuery(id+"F5.imprint","IMPRINT",EDGE,{"disambiguationData":[TD([[subQ270,1.0]])],"derivedFrom":subQ265}),1.0]])]}),makeQuery(id+"F5.imprint","IMPRINT",FACE,{"disambiguationData":[TD([[makeQuery(id+"F5.imprint","IMPRINT",EDGE,{"disambiguationData":[TD([[subQ270,-1.0]])],"derivedFrom":subQ265}),1.0]])]}),makeQuery(id+"F5.imprint","IMPRINT",FACE,{"disambiguationData":[TD([[makeQuery(id+"F5.imprint","IMPRINT",EDGE,{"disambiguationData":[TD([[subQ277,-1.0]])],"derivedFrom":subQ273}),1.0]])]}),makeQuery(id+"F5.imprint","IMPRINT",FACE,{"disambiguationData":[TD([[makeQuery(id+"F5.imprint","IMPRINT",EDGE,{"disambiguationData":[TD([[subQ277,1.0]])],"derivedFrom":subQ273}),1.0]])]}),makeQuery(id+"F5.imprint","IMPRINT",FACE,{"disambiguationData":[TD([[makeQuery(id+"F5.imprint","IMPRINT",EDGE,{"disambiguationData":[TD([[subQ284,-1.0]])],"derivedFrom":subQ279}),1.0]])]}),makeQuery(id+"F5.imprint","IMPRINT",FACE,{"disambiguationData":[TD([[makeQuery(id+"F5.imprint","IMPRINT",EDGE,{"disambiguationData":[TD([[subQ284,1.0]])],"derivedFrom":subQ279}),1.0]])]}),makeQuery(id+"F5.imprint","IMPRINT",FACE,{"disambiguationData":[TD([[makeQuery(id+"F5.imprint","IMPRINT",EDGE,{"disambiguationData":[TD([[subQ291,-1.0]])],"derivedFrom":subQ287}),1.0]])]}),makeQuery(id+"F5.imprint","IMPRINT",FACE,{"disambiguationData":[TD([[makeQuery(id+"F5.imprint","IMPRINT",EDGE,{"disambiguationData":[TD([[subQ291,1.0]])],"derivedFrom":subQ287}),1.0]])]}),makeQuery(id+"F5.imprint","IMPRINT",FACE,{"disambiguationData":[TD([[makeQuery(id+"F5.imprint","IMPRINT",EDGE,{"disambiguationData":[TD([[subQ299,-1.0]])],"derivedFrom":subQ294}),1.0]])]}),makeQuery(id+"F5.imprint","IMPRINT",FACE,{"disambiguationData":[TD([[makeQuery(id+"F5.imprint","IMPRINT",EDGE,{"disambiguationData":[TD([[subQ299,1.0]])],"derivedFrom":subQ294}),1.0]])]}),makeQuery(id+"F5.imprint","IMPRINT",FACE,{"disambiguationData":[TD([[makeQuery(id+"F5.imprint","IMPRINT",EDGE,{"disambiguationData":[TD([[subQ306,1.0]])],"derivedFrom":subQ301}),1.0]])]}),makeQuery(id+"F5.imprint","IMPRINT",FACE,{"disambiguationData":[TD([[makeQuery(id+"F5.imprint","IMPRINT",EDGE,{"disambiguationData":[TD([[subQ306,-1.0]])],"derivedFrom":subQ301}),1.0]])]}),makeQuery(id+"F5.imprint","IMPRINT",FACE,{"disambiguationData":[TD([[makeQuery(id+"F5.imprint","IMPRINT",EDGE,{"disambiguationData":[TD([[subQ314,1.0]])],"derivedFrom":subQ309}),1.0]])]}),makeQuery(id+"F5.imprint","IMPRINT",FACE,{"disambiguationData":[TD([[makeQuery(id+"F5.imprint","IMPRINT",EDGE,{"disambiguationData":[TD([[subQ314,-1.0]])],"derivedFrom":subQ309}),1.0]])]}),makeQuery(id+"F5.imprint","IMPRINT",FACE,{"disambiguationData":[TD([[makeQuery(id+"F5.imprint","IMPRINT",EDGE,{"disambiguationData":[TD([[subQ321,-1.0]])],"derivedFrom":subQ316}),1.0]])]}),makeQuery(id+"F5.imprint","IMPRINT",FACE,{"disambiguationData":[TD([[makeQuery(id+"F5.imprint","IMPRINT",EDGE,{"disambiguationData":[TD([[subQ321,1.0]])],"derivedFrom":subQ316}),1.0]])]}),makeQuery(id+"F5.imprint","IMPRINT",FACE,{"disambiguationData":[TD([[makeQuery(id+"F5.imprint","IMPRINT",EDGE,{"disambiguationData":[TD([[subQ329,1.0]])],"derivedFrom":subQ324}),1.0]])]}),makeQuery(id+"F5.imprint","IMPRINT",FACE,{"disambiguationData":[TD([[makeQuery(id+"F5.imprint","IMPRINT",EDGE,{"disambiguationData":[TD([[subQ329,-1.0]])],"derivedFrom":subQ324}),1.0]])]}),makeQuery(id+"F5.imprint","IMPRINT",FACE,{"disambiguationData":[TD([[makeQuery(id+"F5.imprint","IMPRINT",EDGE,{"disambiguationData":[TD([[subQ336,-1.0]])],"derivedFrom":subQ332}),1.0]])]}),makeQuery(id+"F5.imprint","IMPRINT",FACE,{"disambiguationData":[TD([[makeQuery(id+"F5.imprint","IMPRINT",EDGE,{"disambiguationData":[TD([[subQ336,1.0]])],"derivedFrom":subQ332}),1.0]])]}),makeQuery(id+"F5.imprint","IMPRINT",FACE,{"disambiguationData":[TD([[makeQuery(id+"F5.imprint","IMPRINT",EDGE,{"disambiguationData":[TD([[subQ343,-1.0]])],"derivedFrom":subQ338}),1.0]])]}),makeQuery(id+"F5.imprint","IMPRINT",FACE,{"disambiguationData":[TD([[makeQuery(id+"F5.imprint","IMPRINT",EDGE,{"disambiguationData":[TD([[subQ343,1.0]])],"derivedFrom":subQ338}),1.0]])]}),makeQuery(id+"F5.imprint","IMPRINT",FACE,{"disambiguationData":[TD([[makeQuery(id+"F5.imprint","IMPRINT",EDGE,{"disambiguationData":[TD([[subQ350,-1.0]])],"derivedFrom":subQ346}),1.0]])]}),makeQuery(id+"F5.imprint","IMPRINT",FACE,{"disambiguationData":[TD([[makeQuery(id+"F5.imprint","IMPRINT",EDGE,{"disambiguationData":[TD([[subQ350,1.0]])],"derivedFrom":subQ346}),1.0]])]})]);}
            extrude(context, id + "F6", {"entities" : qUnion([Q0]), "operationType" : NewBodyOperationType.REMOVE, "oppositeDirection" : true, "depth" : 25 * mm});
        }
    });
